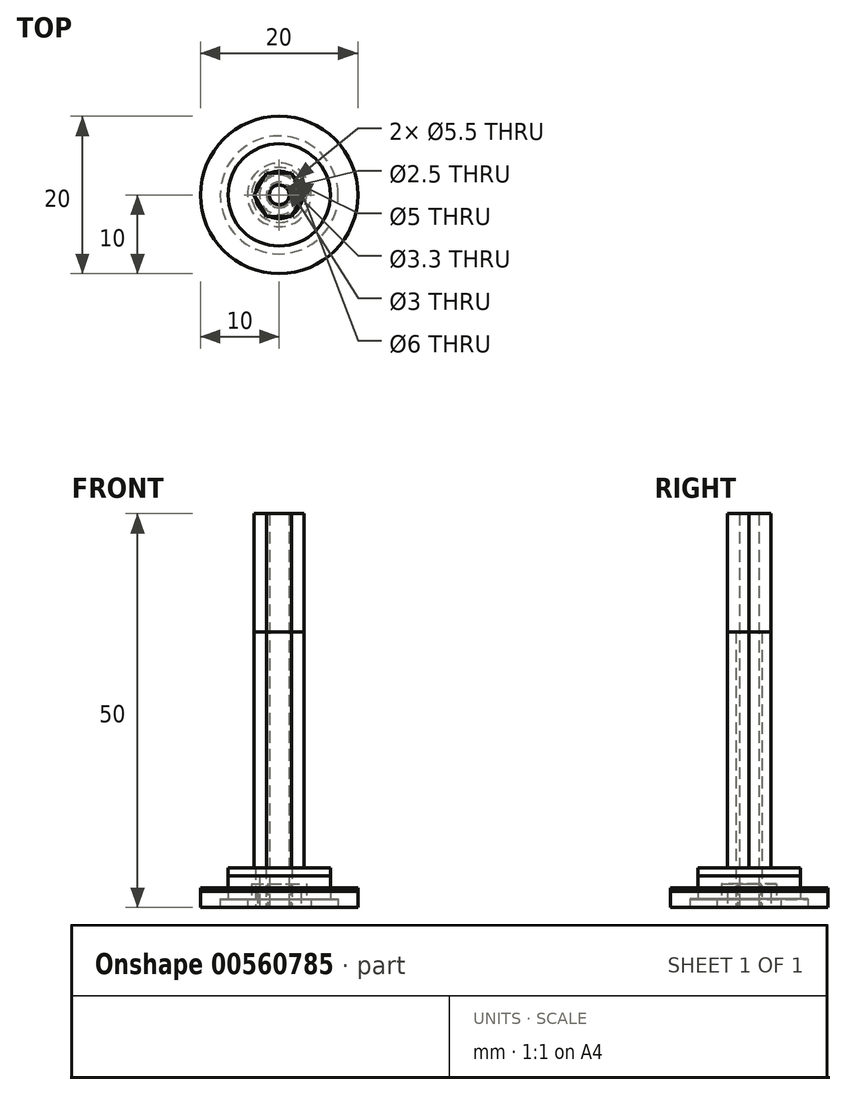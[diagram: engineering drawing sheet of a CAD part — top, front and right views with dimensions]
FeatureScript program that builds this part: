
annotation { "Feature Type Name" : "Feature", "Feature Type Description" : "" }
export const myFeature = defineFeature(function(context is Context, id is Id, definition is map)
    precondition{}
    {
        {
            var Q0;
            Q0=qCreatedBy(makeId("Top.planeOp"),FACE);
            var sketch = newSketch(context, id + "F0", { "sketchPlane" : qUnion([Q0])});
            skCircle(sketch, "E0.cCircle", {"center": v(0, 0) * mm, "radius": 2.75 * mm, "construction": true});
            skLineSegment(sketch, "E0.0", {"start": v(1.59, -2.75) * mm, "end": v(-1.59, -2.75) * mm});
            skLineSegment(sketch, "E0.1", {"start": v(-1.59, -2.75) * mm, "end": v(-3.18, 0) * mm});
            skLineSegment(sketch, "E0.2", {"start": v(-3.18, 0) * mm, "end": v(-1.59, 2.75) * mm});
            skLineSegment(sketch, "E0.3", {"start": v(-1.59, 2.75) * mm, "end": v(1.59, 2.75) * mm});
            skLineSegment(sketch, "E0.4", {"start": v(1.59, 2.75) * mm, "end": v(3.18, 0) * mm});
            skLineSegment(sketch, "E0.5", {"start": v(3.18, 0) * mm, "end": v(1.59, -2.75) * mm});
            skPoint(sketch, "E0.0.midPoint", {"position": v(0, -2.75) * mm});
            skSolve(sketch);
        }
        {
            var Q0;
            Q0=makeQuery(id+"F0.imprint","IMPRINT",FACE,{"disambiguationData":[TD([[makeQuery(id+"F0.imprint","IMPRINT",EDGE,{"derivedFrom":sQuery(id+"F0.wireOp",EDGE,"E0.0")}),-1.0]])]});
            extrude(context, id + "F1", {"entities" : qUnion([Q0]), "depth" : 50 * mm});
        }
        {
            var Q0;
            Q0=sQuery(id+"F0.wireOp",VERTEX,"E0.cCircle.center");
            var Q1;
            Q1=makeQuery(id+"F1.opExtrude","SWEPT_BODY",BODY,{"disambiguationData":[OSD([sQuery(id+"F0.wireOp",EDGE,"E0.0"),sQuery(id+"F0.wireOp",EDGE,"E0.1"),sQuery(id+"F0.wireOp",EDGE,"E0.2"),sQuery(id+"F0.wireOp",EDGE,"E0.3"),sQuery(id+"F0.wireOp",EDGE,"E0.4"),sQuery(id+"F0.wireOp",EDGE,"E0.5")])]});
            hole(context, id + "F2", {"style" : HoleStyle.SIMPLE, "endStyle" : HoleEndStyle.THROUGH, "oppositeDirection" : true, "standardTappedOrClearance" : lookupTablePath({ "standard" : "ISO", "engagement" : "75%", "pitch" : "0.5 mm", "size" : "M3", "type" : "Tapped" }), "standardBlindInLast" : lookupTablePath({ "standard" : "ISO", "engagement" : "75%", "pitch" : "0.5 mm", "size" : "M3", "type" : "Tapped" }), "holeDiameter" : 2.5 * mm, "showTappedDepth" : true, "isTappedThrough" : true, "tappedDepth" : 6.2 * mm, "tapClearance" : 3, "locations" : qUnion([Q0]), "scope" : qUnion([Q1]), "majorDiameter" : 3 * mm});
        }
        {
            var Q0;
            Q0=qCreatedBy(makeId("Front.planeOp"),FACE);
            var sketch = newSketch(context, id + "F3", { "sketchPlane" : qUnion([Q0])});
            skLineSegment(sketch, "E1", {"start": v(0, 0) * mm, "end": v(0, 7.5) * mm, "construction": true});
            skLineSegment(sketch, "E2", {"start": v(-6.5, 5) * mm, "end": v(-6.5, 1.1) * mm});
            skLineSegment(sketch, "E3", {"start": v(-6.5, 1.1) * mm, "end": v(-7.5, 1.1) * mm});
            skLineSegment(sketch, "E4", {"start": v(-7.5, 1.1) * mm, "end": v(-7.5, 0) * mm});
            skLineSegment(sketch, "E5", {"start": v(-6.5, 5) * mm, "end": v(-3, 5) * mm});
            skLineSegment(sketch, "E6", {"start": v(-7.5, 0) * mm, "end": v(-3, 0) * mm});
            skLineSegment(sketch, "E7", {"start": v(-3, 0) * mm, "end": v(-3, 5) * mm});
            skSolve(sketch);
        }
        {
            var Q0;
            Q0=qSketchRegion(id+"F3",true);
            var Q1;
            Q1=sQuery(id+"F3.wireOp",EDGE,"E1");
            revolve(context, id + "F4", {"entities" : qUnion([Q0]), "axis" : qUnion([Q1]), "revolveType" : RevolveType.FULL});
        }
        {
            var Q0;
            Q0=qCreatedBy(makeId("Front.planeOp"),FACE);
            var sketch = newSketch(context, id + "F5", { "sketchPlane" : qUnion([Q0])});
            skLineSegment(sketch, "E8", {"start": v(0, 0) * mm, "end": v(0, 7.1) * mm, "construction": true});
            skLineSegment(sketch, "E9", {"start": v(-2.5, 0) * mm, "end": v(-2.5, 4) * mm});
            skLineSegment(sketch, "E10", {"start": v(-2.5, 4) * mm, "end": v(-6.5, 4) * mm});
            skLineSegment(sketch, "E11", {"start": v(-6.5, 4) * mm, "end": v(-6.5, 1) * mm});
            skLineSegment(sketch, "E12", {"start": v(-6.5, 1) * mm, "end": v(-7.5, 1) * mm});
            skLineSegment(sketch, "E13", {"start": v(-7.5, 1) * mm, "end": v(-7.5, 0) * mm});
            skLineSegment(sketch, "E14", {"start": v(-7.5, 0) * mm, "end": v(-2.5, 0) * mm});
            skSolve(sketch);
        }
        {
            var Q0;
            Q0=qSketchRegion(id+"F5",true);
            var Q1;
            Q1=sQuery(id+"F5.wireOp",EDGE,"E8");
            revolve(context, id + "F6", {"entities" : qUnion([Q0]), "axis" : qUnion([Q1]), "revolveType" : RevolveType.FULL});
        }
        {
            var Q0;
            Q0=qSketchRegion(id+"F0",true);
            extrude(context, id + "F7", {"entities" : qUnion([Q0]), "depth" : 35 * mm});
        }
        {
            var Q0;
            Q0=sQuery(id+"F0.wireOp",VERTEX,"E0.cCircle.center");
            var Q1;
            Q1=makeQuery(id+"F7.opExtrude","SWEPT_BODY",BODY,{"disambiguationData":[OSD([sQuery(id+"F0.wireOp",EDGE,"E0.0"),sQuery(id+"F0.wireOp",EDGE,"E0.1"),sQuery(id+"F0.wireOp",EDGE,"E0.2"),sQuery(id+"F0.wireOp",EDGE,"E0.3"),sQuery(id+"F0.wireOp",EDGE,"E0.4"),sQuery(id+"F0.wireOp",EDGE,"E0.5")])]});
            hole(context, id + "F8", {"style" : HoleStyle.SIMPLE, "endStyle" : HoleEndStyle.THROUGH, "oppositeDirection" : true, "standardTappedOrClearance" : lookupTablePath({ "standard" : "ISO", "fit" : "Normal", "size" : "M3", "type" : "Clearance" }), "standardBlindInLast" : lookupTablePath({ "fit" : "Standard", "standard" : "ISO", "size" : "M3", "type" : "Clearance" }), "holeDiameter" : 3.3 * mm, "isTappedThrough" : true, "tappedDepth" : 6.2 * mm, "tapClearance" : 3, "locations" : qUnion([Q0]), "scope" : qUnion([Q1])});
        }
        {
            var Q0;
            Q0=qCreatedBy(makeId("Front.planeOp"),FACE);
            var sketch = newSketch(context, id + "F9", { "sketchPlane" : qUnion([Q0])});
            skLineSegment(sketch, "E15", {"start": v(0, 0) * mm, "end": v(0, 4.3) * mm, "construction": true});
            skLineSegment(sketch, "E16", {"start": v(-1.5, 0) * mm, "end": v(-1.5, 3) * mm});
            skLineSegment(sketch, "E17", {"start": v(-1.5, 3) * mm, "end": v(-3.5, 3) * mm});
            skLineSegment(sketch, "E18", {"start": v(-3.5, 3) * mm, "end": v(-3.5, 1) * mm});
            skLineSegment(sketch, "E19", {"start": v(-3.5, 1) * mm, "end": v(-4.05, 1) * mm});
            skLineSegment(sketch, "E20", {"start": v(-4.05, 1) * mm, "end": v(-4.05, 0) * mm});
            skLineSegment(sketch, "E21", {"start": v(-4.05, 0) * mm, "end": v(-1.5, 0) * mm});
            skSolve(sketch);
        }
        {
            var Q0;
            Q0=makeQuery(id+"F9.imprint","IMPRINT",FACE,{"disambiguationData":[TD([[makeQuery(id+"F9.imprint","IMPRINT",EDGE,{"derivedFrom":sQuery(id+"F9.wireOp",EDGE,"E16")}),1.0]])]});
            var Q1;
            Q1=sQuery(id+"F9.wireOp",EDGE,"E15");
            revolve(context, id + "F10", {"entities" : qUnion([Q0]), "axis" : qUnion([Q1]), "revolveType" : RevolveType.FULL});
        }
        {
            var Q0;
            Q0=qCreatedBy(makeId("Top.planeOp"),FACE);
            var sketch = newSketch(context, id + "F11", { "sketchPlane" : qUnion([Q0])});
            skCircle(sketch, "E22", {"center": v(0, 0) * mm, "radius": 10 * mm});
            skCircle(sketch, "E23", {"center": v(0, 0) * mm, "radius": 2.75 * mm});
            skSolve(sketch);
        }
        {
            var Q0;
            Q0=makeQuery(id+"F11.imprint","IMPRINT",FACE,{"disambiguationData":[TD([[makeQuery(id+"F11.imprint","IMPRINT",EDGE,{"derivedFrom":sQuery(id+"F11.wireOp",EDGE,"E22")}),1.0]])]});
            extrude(context, id + "F12", {"entities" : qUnion([Q0]), "depth" : 2.5 * mm});
        }
        {
            var Q0;
            Q0=qSketchRegion(id+"F11",true);
            extrude(context, id + "F13", {"entities" : qUnion([Q0]), "depth" : 2 * mm});
        }
    });
